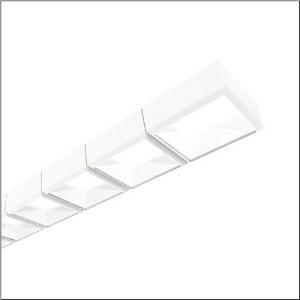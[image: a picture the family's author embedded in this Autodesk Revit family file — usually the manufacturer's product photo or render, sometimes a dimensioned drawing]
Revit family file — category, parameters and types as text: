
# Revit family: scriptus_r__11_5mz212d03wa_20e5
name_source: partatom
category: Lighting Fixtures
units: mm (PartAtom-declared; Revit-internal decimal feet)

## family parameters
Cut with Voids When Loaded = No
Host = Face
Light Source = No
Part Type = Normal
Room Calculation Point = No
Round Connector Dimension = Use Diameter
Shared = No

## types (1)
- Scriptus® 11 (1 x LED 3000K / CRI = 80 (unbekannt), 2200 lm, 3000K)
    Apparent Load = 35 VA
    CIE Flux Codes = 82 95 99 100 100
    Color Rendering = 80
    Color Temperature = 3000K
    Default Elevation = 1800 mm
    Description = Scriptus® 11, office luminaire, primary optical cover: lenses, CAT 2 (L<= 3000cd/m²), light emission: direct distribution, primary light characteristic: symmetric, installation type: surface-mounted, LED rated luminous flux: 4.390 lm, light colour: 830, colour temperature: 3000K, control gear: ECG DALI, with terminal, 5-pole, mains connection: 230V, AC, 50Hz, rated input power: 35W, housing, luminaire housing, of aluminium, traffic white (RAL 9016), length: 1.658 mm, width: 114 mm, height: 57mm, protection rating (complete): IP20, insulation class (complete): insulation class I (protective earthing), certification: CE, ENEC, VDE, protection symbol: F, permissible ambient temperature for indoor applications: 0..+35°C, standard: EN 50419, packaging unit: 1 piece
    Height = 57 mm
    Lamp = 1 x LED 3000K / CRI >= 80 (unbekannt)
    Lamp Light Flux = 2200 lm
    Lamp count = 1
    Length = 1658 mm
    Luminous efficacy = 127 lm/W
    Manufacturer = Siteco
    ModVariant = No
    Model = 5MZ212D03WA
    Mounting Place = Ceiling
    Mounting Type = Surface mounted
    Number of Poles = 1
    OnlyDefault = Yes
    Power Factor = 1
    Product Name = Scriptus® 11
    Product group = office luminaire | ceiling mounted
    ProductGroupID = 302
    Protection Class = Protection class I
    Protection Degree = IP 20
    RLX_Detail_Level = 1
    RlxData = <blob elided: 29481 chars, md5=1100a81a>
    Socket = socket
    Standby Power = 0 W
    System Light Flux = 4400 lm
    System Power = 35 W
    Type Comments = Product without accessories
    Type Image = l_1004833.jpg
    URL = http://relux.com
    VarID = ---
    Voltage = 0 V
    Weight = 0.00 kg
    Width = 114 mm

## geometry (parser evidence)
native form markers: Blend x4, Sweep x13
no freeform markers — native parametric forms only
